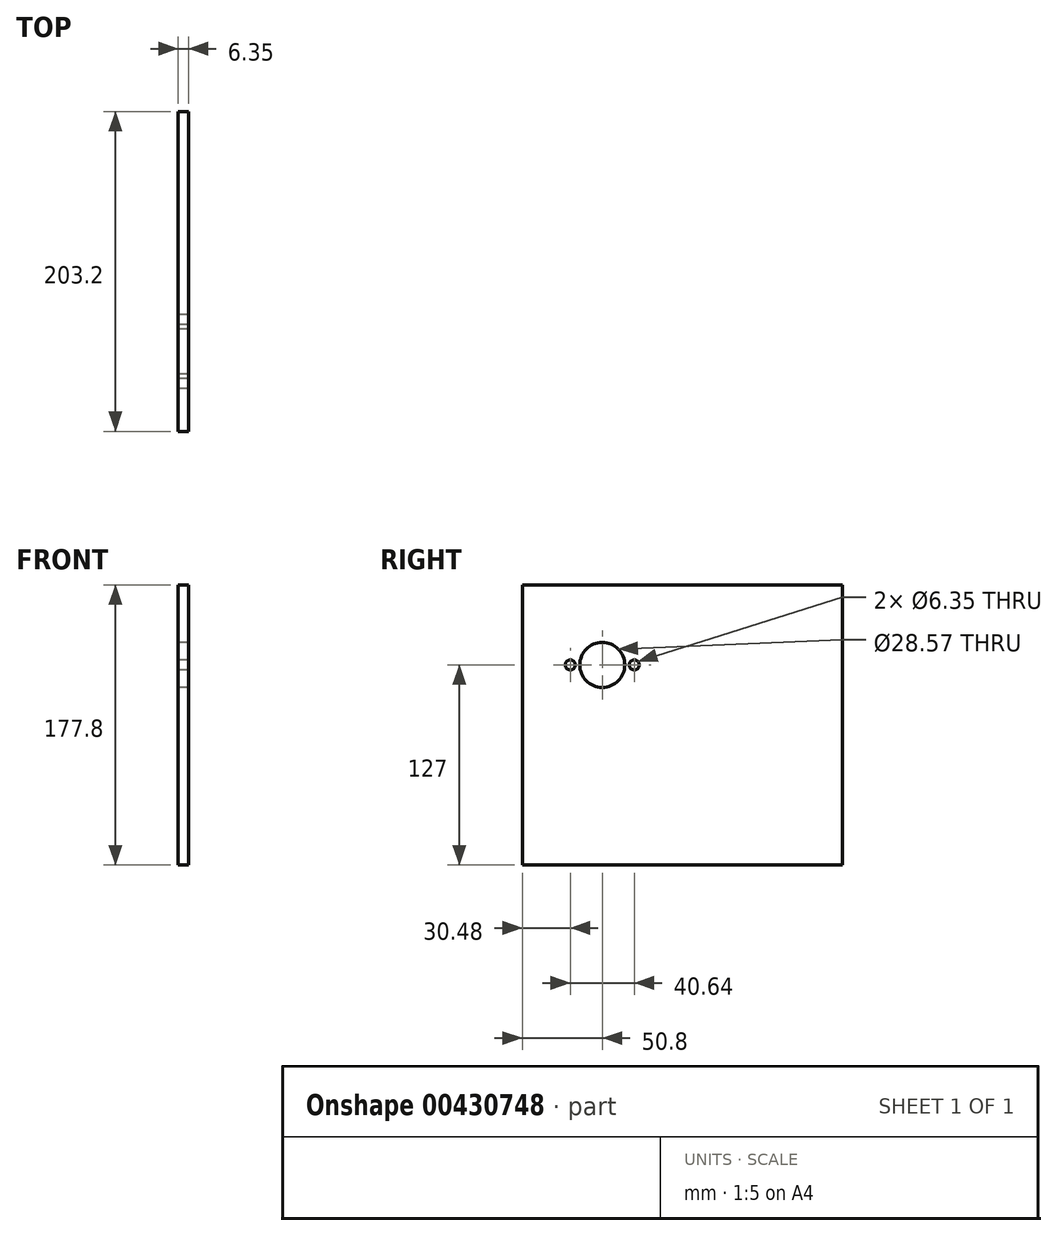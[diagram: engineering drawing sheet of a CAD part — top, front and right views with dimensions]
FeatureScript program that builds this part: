
annotation { "Feature Type Name" : "Feature", "Feature Type Description" : "" }
export const myFeature = defineFeature(function(context is Context, id is Id, definition is map)
    precondition{}
    {
        {
            var Q0;
            Q0=qCreatedBy(makeId("Right.planeOp"),FACE);
            var sketch = newSketch(context, id + "F0", { "sketchPlane" : qUnion([Q0])});
            skLineSegment(sketch, "E0", {"start": v(0, 0) * mm, "end": v(0, 177.8) * mm});
            skLineSegment(sketch, "E1", {"start": v(0, 177.8) * mm, "end": v(203.2, 177.8) * mm});
            skCircle(sketch, "E2", {"center": v(50.8, 127) * mm, "radius": 14.29 * mm});
            skLineSegment(sketch, "E3", {"start": v(0, 0) * mm, "end": v(203.2, 0) * mm});
            skLineSegment(sketch, "E4", {"start": v(203.2, 0) * mm, "end": v(203.2, 177.8) * mm});
            skCircle(sketch, "E5", {"center": v(71.12, 127) * mm, "radius": 3.18 * mm});
            skCircle(sketch, "E6", {"center": v(30.48, 127) * mm, "radius": 3.18 * mm});
            skLineSegment(sketch, "E7", {"start": v(71.12, 127) * mm, "end": v(30.48, 127) * mm, "construction": true});
            skSolve(sketch);
        }
        {
            var Q0;
            Q0=makeQuery(id+"F0.imprint","IMPRINT",FACE,{"disambiguationData":[TD([[makeQuery(id+"F0.imprint","IMPRINT",EDGE,{"derivedFrom":sQuery(id+"F0.wireOp",EDGE,"E0")}),-1.0]])]});
            extrude(context, id + "F1", {"entities" : qUnion([Q0]), "depth" : 6.35 * mm, "offsetDistance" : 25.4 * mm});
        }
    });
